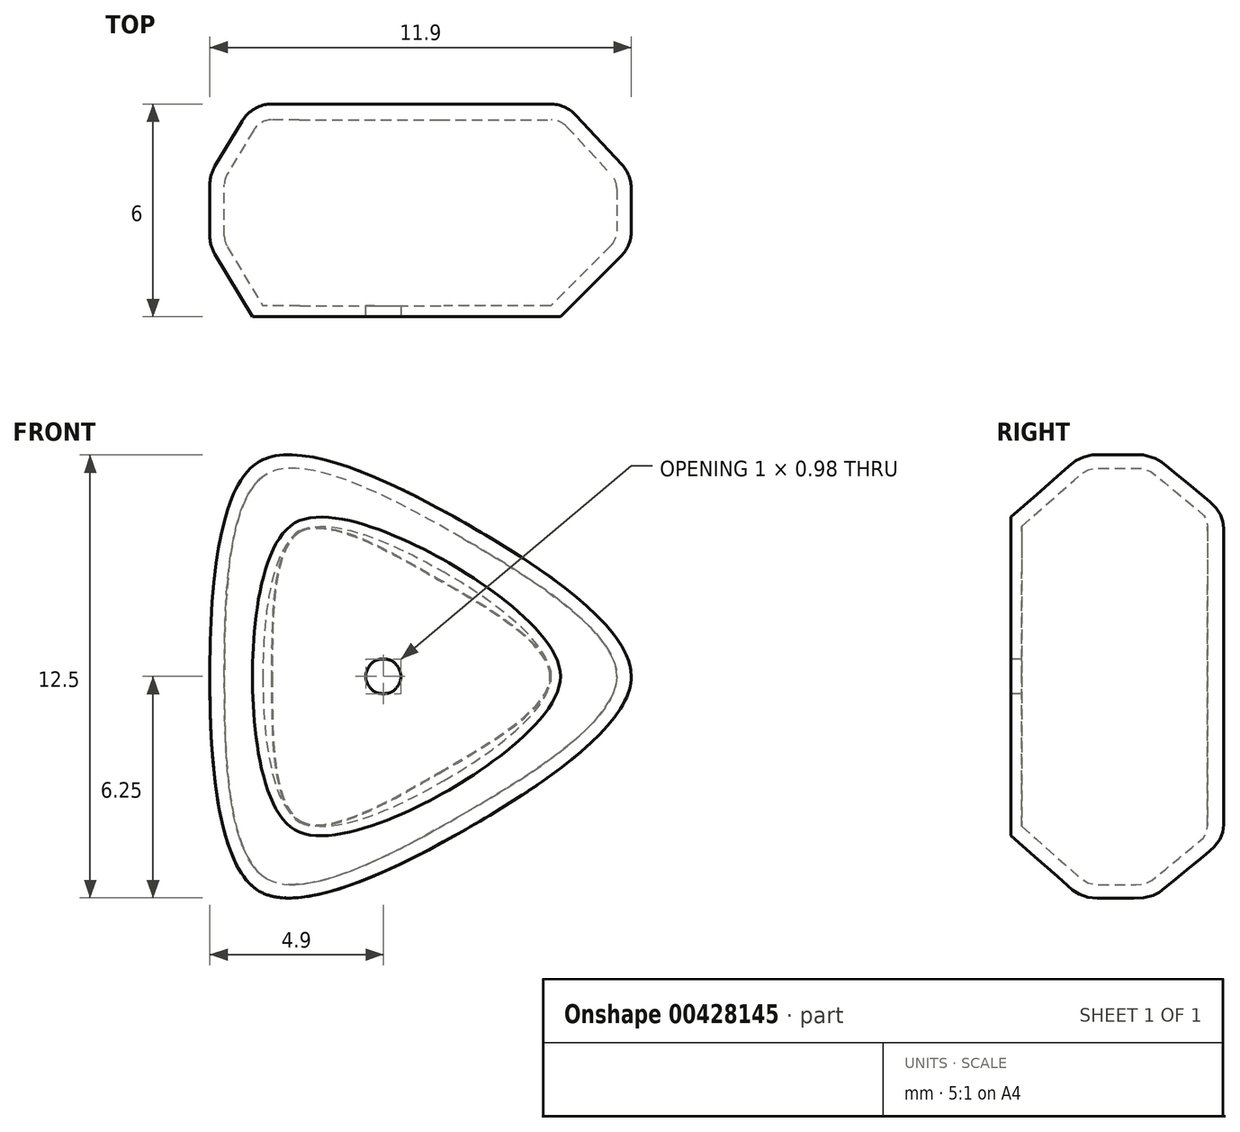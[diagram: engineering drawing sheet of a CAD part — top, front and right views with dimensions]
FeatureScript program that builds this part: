
annotation { "Feature Type Name" : "Feature", "Feature Type Description" : "" }
export const myFeature = defineFeature(function(context is Context, id is Id, definition is map)
    precondition{}
    {
        {
            var Q0;
            Q0=qCreatedBy(makeId("Top.planeOp"),FACE);
            var sketch = newSketch(context, id + "F0", { "sketchPlane" : qUnion([Q0])});
            skLineSegment(sketch, "E0", {"start": v(0, 0) * mm, "end": v(0, 3) * mm});
            skSolve(sketch);
        }
        {
            var Q0;
            Q0=sQuery(id+"F0.wireOp",EDGE,"E0");
            cPlane(context, id + "F1", {"entities" : qUnion([Q0]), "cplaneType" : CPlaneType.LINE_ANGLE, "offset" : 25 * mm, "angle" : 120 * degree, "width" : 150 * mm, "height" : 150 * mm});
        }
        {
            var Q0;
            Q0=sQuery(id+"F0.wireOp",EDGE,"E0");
            cPlane(context, id + "F2", {"entities" : qUnion([Q0]), "cplaneType" : CPlaneType.LINE_ANGLE, "offset" : 25 * mm, "angle" : 120 * degree, "oppositeDirection" : true, "width" : 150 * mm, "height" : 150 * mm});
        }
        {
            var Q0;
            Q0=qCreatedBy(makeId("Top.planeOp"),FACE);
            var sketch = newSketch(context, id + "F3", { "sketchPlane" : qUnion([Q0])});
            skLineSegment(sketch, "E1", {"start": v(0.5, 0) * mm, "end": v(5, 0) * mm});
            skLineSegment(sketch, "E2", {"start": v(7, 2.41) * mm, "end": v(7, 3.6) * mm});
            skLineSegment(sketch, "E3", {"start": v(4.7, 6) * mm, "end": v(0.5, 6) * mm});
            skLineSegment(sketch, "E4", {"start": v(5.44, 5.68) * mm, "end": v(6.73, 4.29) * mm});
            skLineSegment(sketch, "E5", {"start": v(6.7, 1.7) * mm, "end": v(5, 0) * mm});
            skLineSegment(sketch, "E6", {"start": v(0.5, 6) * mm, "end": v(0.5, 5.55) * mm});
            skLineSegment(sketch, "E7", {"start": v(0.5, 5.55) * mm, "end": v(4.74, 5.55) * mm});
            skLineSegment(sketch, "E8", {"start": v(6.6, 3.6) * mm, "end": v(6.6, 2.41) * mm});
            skLineSegment(sketch, "E9", {"start": v(4.72, 0.3) * mm, "end": v(0.5, 0.3) * mm});
            skLineSegment(sketch, "E10", {"start": v(5.18, 5.36) * mm, "end": v(6.43, 4) * mm});
            skLineSegment(sketch, "E11", {"start": v(6.42, 2) * mm, "end": v(4.72, 0.3) * mm});
            skPoint(sketch, "E12.visualSharp", {"position": v(5.14, 6) * mm});
            skArc(sketch, "E12.filletArc", {"start": v(5.44, 5.68) * mm, "mid": v(5.1, 5.92) * mm, "end": v(4.7, 6) * mm});
            skPoint(sketch, "E13.visualSharp", {"position": v(7, 4) * mm});
            skArc(sketch, "E13.filletArc", {"start": v(7, 3.6) * mm, "mid": v(6.93, 3.97) * mm, "end": v(6.73, 4.29) * mm});
            skPoint(sketch, "E14.visualSharp", {"position": v(7, 2) * mm});
            skArc(sketch, "E14.filletArc", {"start": v(6.7, 1.7) * mm, "mid": v(6.92, 2.03) * mm, "end": v(7, 2.41) * mm});
            skPoint(sketch, "E15.visualSharp", {"position": v(5, 5.55) * mm});
            skArc(sketch, "E15.filletArc", {"start": v(5.18, 5.36) * mm, "mid": v(4.98, 5.5) * mm, "end": v(4.74, 5.55) * mm});
            skPoint(sketch, "E16.visualSharp", {"position": v(6.6, 3.84) * mm});
            skArc(sketch, "E16.filletArc", {"start": v(6.6, 3.6) * mm, "mid": v(6.55, 3.82) * mm, "end": v(6.43, 4) * mm});
            skPoint(sketch, "E17.visualSharp", {"position": v(6.6, 2.17) * mm});
            skArc(sketch, "E17.filletArc", {"start": v(6.42, 2) * mm, "mid": v(6.55, 2.19) * mm, "end": v(6.6, 2.41) * mm});
            skLineSegment(sketch, "E18", {"start": v(0.5, 0.3) * mm, "end": v(0.5, 0) * mm});
            skSolve(sketch);
        }
        {
            var Q0;
            Q0=qCreatedBy(makeId("Top.planeOp"),FACE);
            var sketch = newSketch(context, id + "F4", { "sketchPlane" : qUnion([Q0])});
            skLineSegment(sketch, "E19", {"start": v(-0.5, 0) * mm, "end": v(-3.7, 0) * mm});
            skLineSegment(sketch, "E20", {"start": v(-4.9, 2.28) * mm, "end": v(-4.9, 3.72) * mm});
            skLineSegment(sketch, "E21", {"start": v(-4.76, 1.76) * mm, "end": v(-3.7, 0) * mm});
            skLineSegment(sketch, "E22", {"start": v(-3.13, 6) * mm, "end": v(-0.5, 6) * mm});
            skLineSegment(sketch, "E23", {"start": v(-4.76, 4.24) * mm, "end": v(-4, 5.51) * mm});
            skLineSegment(sketch, "E24", {"start": v(-0.5, 0) * mm, "end": v(-0.5, 0.3) * mm});
            skLineSegment(sketch, "E25", {"start": v(-0.5, 0.3) * mm, "end": v(-3.4, 0.3) * mm});
            skLineSegment(sketch, "E26", {"start": v(-4.5, 2.28) * mm, "end": v(-4.5, 3.72) * mm});
            skLineSegment(sketch, "E27", {"start": v(-3.16, 5.55) * mm, "end": v(-0.5, 5.55) * mm});
            skLineSegment(sketch, "E28", {"start": v(-0.5, 5.55) * mm, "end": v(-0.5, 6) * mm});
            skLineSegment(sketch, "E29", {"start": v(-3.66, 5.26) * mm, "end": v(-4.4, 4.03) * mm});
            skLineSegment(sketch, "E30", {"start": v(-4.4, 1.97) * mm, "end": v(-3.4, 0.3) * mm});
            skPoint(sketch, "E31.visualSharp", {"position": v(-3.7, 6) * mm});
            skArc(sketch, "E31.filletArc", {"start": v(-3.13, 6) * mm, "mid": v(-3.63, 5.87) * mm, "end": v(-4, 5.51) * mm});
            skPoint(sketch, "E32.visualSharp", {"position": v(-4.9, 4) * mm});
            skArc(sketch, "E32.filletArc", {"start": v(-4.76, 4.24) * mm, "mid": v(-4.86, 3.99) * mm, "end": v(-4.9, 3.72) * mm});
            skPoint(sketch, "E33.visualSharp", {"position": v(-4.9, 2) * mm});
            skArc(sketch, "E33.filletArc", {"start": v(-4.9, 2.28) * mm, "mid": v(-4.86, 2.01) * mm, "end": v(-4.76, 1.76) * mm});
            skPoint(sketch, "E34.visualSharp", {"position": v(-3.5, 5.55) * mm});
            skArc(sketch, "E34.filletArc", {"start": v(-3.16, 5.55) * mm, "mid": v(-3.45, 5.47) * mm, "end": v(-3.66, 5.26) * mm});
            skPoint(sketch, "E35.visualSharp", {"position": v(-4.5, 3.89) * mm});
            skArc(sketch, "E35.filletArc", {"start": v(-4.4, 4.03) * mm, "mid": v(-4.47, 3.88) * mm, "end": v(-4.5, 3.72) * mm});
            skPoint(sketch, "E36.visualSharp", {"position": v(-4.5, 2.11) * mm});
            skArc(sketch, "E36.filletArc", {"start": v(-4.5, 2.28) * mm, "mid": v(-4.47, 2.12) * mm, "end": v(-4.4, 1.97) * mm});
            skSolve(sketch);
        }
        {
            var Q0;
            Q0=qCreatedBy(id+"F2.planeOp",FACE);
            var sketch = newSketch(context, id + "F5", { "sketchPlane" : qUnion([Q0])});
            skLineSegment(sketch, "E37", {"start": v(0, 0.5) * mm, "end": v(0, 5) * mm});
            skLineSegment(sketch, "E38", {"start": v(-2.41, 7) * mm, "end": v(-3.6, 7) * mm});
            skLineSegment(sketch, "E39", {"start": v(-6, 4.7) * mm, "end": v(-6, 0.5) * mm});
            skLineSegment(sketch, "E40", {"start": v(-5.68, 5.44) * mm, "end": v(-4.29, 6.73) * mm});
            skLineSegment(sketch, "E41", {"start": v(-1.7, 6.7) * mm, "end": v(0, 5) * mm});
            skLineSegment(sketch, "E42", {"start": v(-6, 0.5) * mm, "end": v(-5.55, 0.5) * mm});
            skLineSegment(sketch, "E43", {"start": v(-5.55, 0.5) * mm, "end": v(-5.55, 4.74) * mm});
            skLineSegment(sketch, "E44", {"start": v(-3.6, 6.6) * mm, "end": v(-2.41, 6.6) * mm});
            skLineSegment(sketch, "E45", {"start": v(-0.3, 4.72) * mm, "end": v(-0.3, 0.5) * mm});
            skLineSegment(sketch, "E46", {"start": v(-5.36, 5.18) * mm, "end": v(-4, 6.43) * mm});
            skLineSegment(sketch, "E47", {"start": v(-2, 6.42) * mm, "end": v(-0.3, 4.72) * mm});
            skPoint(sketch, "E48.visualSharp", {"position": v(-6, 5.14) * mm});
            skArc(sketch, "E48.filletArc", {"start": v(-5.68, 5.44) * mm, "mid": v(-5.92, 5.1) * mm, "end": v(-6, 4.7) * mm});
            skPoint(sketch, "E49.visualSharp", {"position": v(-4, 7) * mm});
            skArc(sketch, "E49.filletArc", {"start": v(-3.6, 7) * mm, "mid": v(-3.97, 6.93) * mm, "end": v(-4.29, 6.73) * mm});
            skPoint(sketch, "E50.visualSharp", {"position": v(-2, 7) * mm});
            skArc(sketch, "E50.filletArc", {"start": v(-1.7, 6.7) * mm, "mid": v(-2.03, 6.92) * mm, "end": v(-2.41, 7) * mm});
            skPoint(sketch, "E51.visualSharp", {"position": v(-5.55, 5) * mm});
            skArc(sketch, "E51.filletArc", {"start": v(-5.36, 5.18) * mm, "mid": v(-5.5, 4.98) * mm, "end": v(-5.55, 4.74) * mm});
            skPoint(sketch, "E52.visualSharp", {"position": v(-3.84, 6.6) * mm});
            skArc(sketch, "E52.filletArc", {"start": v(-3.6, 6.6) * mm, "mid": v(-3.82, 6.55) * mm, "end": v(-4, 6.43) * mm});
            skPoint(sketch, "E53.visualSharp", {"position": v(-2.17, 6.6) * mm});
            skArc(sketch, "E53.filletArc", {"start": v(-2, 6.42) * mm, "mid": v(-2.19, 6.55) * mm, "end": v(-2.41, 6.6) * mm});
            skLineSegment(sketch, "E54", {"start": v(-0.3, 0.5) * mm, "end": v(0, 0.5) * mm});
            skSolve(sketch);
        }
        {
            var Q0;
            Q0=qCreatedBy(id+"F2.planeOp",FACE);
            var sketch = newSketch(context, id + "F6", { "sketchPlane" : qUnion([Q0])});
            skLineSegment(sketch, "E55", {"start": v(0, -0.5) * mm, "end": v(0, -3.7) * mm});
            skLineSegment(sketch, "E56", {"start": v(-2.28, -4.9) * mm, "end": v(-3.72, -4.9) * mm});
            skLineSegment(sketch, "E57", {"start": v(-1.76, -4.76) * mm, "end": v(0, -3.7) * mm});
            skLineSegment(sketch, "E58", {"start": v(-6, -3.13) * mm, "end": v(-6, -0.5) * mm});
            skLineSegment(sketch, "E59", {"start": v(-4.24, -4.76) * mm, "end": v(-5.51, -4) * mm});
            skLineSegment(sketch, "E60", {"start": v(0, -0.5) * mm, "end": v(-0.3, -0.5) * mm});
            skLineSegment(sketch, "E61", {"start": v(-0.3, -0.5) * mm, "end": v(-0.3, -3.4) * mm});
            skLineSegment(sketch, "E62", {"start": v(-2.28, -4.5) * mm, "end": v(-3.72, -4.5) * mm});
            skLineSegment(sketch, "E63", {"start": v(-5.55, -3.16) * mm, "end": v(-5.55, -0.5) * mm});
            skLineSegment(sketch, "E64", {"start": v(-5.55, -0.5) * mm, "end": v(-6, -0.5) * mm});
            skLineSegment(sketch, "E65", {"start": v(-5.26, -3.66) * mm, "end": v(-4.03, -4.4) * mm});
            skLineSegment(sketch, "E66", {"start": v(-1.97, -4.4) * mm, "end": v(-0.3, -3.4) * mm});
            skPoint(sketch, "E67.visualSharp", {"position": v(-6, -3.7) * mm});
            skArc(sketch, "E67.filletArc", {"start": v(-6, -3.13) * mm, "mid": v(-5.87, -3.63) * mm, "end": v(-5.51, -4) * mm});
            skPoint(sketch, "E68.visualSharp", {"position": v(-4, -4.9) * mm});
            skArc(sketch, "E68.filletArc", {"start": v(-4.24, -4.76) * mm, "mid": v(-3.99, -4.86) * mm, "end": v(-3.72, -4.9) * mm});
            skPoint(sketch, "E69.visualSharp", {"position": v(-2, -4.9) * mm});
            skArc(sketch, "E69.filletArc", {"start": v(-2.28, -4.9) * mm, "mid": v(-2.01, -4.86) * mm, "end": v(-1.76, -4.76) * mm});
            skPoint(sketch, "E70.visualSharp", {"position": v(-5.55, -3.5) * mm});
            skArc(sketch, "E70.filletArc", {"start": v(-5.55, -3.16) * mm, "mid": v(-5.47, -3.45) * mm, "end": v(-5.26, -3.66) * mm});
            skPoint(sketch, "E71.visualSharp", {"position": v(-3.89, -4.5) * mm});
            skArc(sketch, "E71.filletArc", {"start": v(-4.03, -4.4) * mm, "mid": v(-3.88, -4.47) * mm, "end": v(-3.72, -4.5) * mm});
            skPoint(sketch, "E72.visualSharp", {"position": v(-2.11, -4.5) * mm});
            skArc(sketch, "E72.filletArc", {"start": v(-2.28, -4.5) * mm, "mid": v(-2.12, -4.47) * mm, "end": v(-1.97, -4.4) * mm});
            skSolve(sketch);
        }
        {
            var Q0;
            Q0=qCreatedBy(id+"F1.planeOp",FACE);
            var sketch = newSketch(context, id + "F7", { "sketchPlane" : qUnion([Q0])});
            skLineSegment(sketch, "E73", {"start": v(0, -0.5) * mm, "end": v(0, -5) * mm});
            skLineSegment(sketch, "E74", {"start": v(2.41, -7) * mm, "end": v(3.6, -7) * mm});
            skLineSegment(sketch, "E75", {"start": v(6, -4.7) * mm, "end": v(6, -0.5) * mm});
            skLineSegment(sketch, "E76", {"start": v(5.68, -5.44) * mm, "end": v(4.29, -6.73) * mm});
            skLineSegment(sketch, "E77", {"start": v(1.7, -6.7) * mm, "end": v(0, -5) * mm});
            skLineSegment(sketch, "E78", {"start": v(6, -0.5) * mm, "end": v(5.55, -0.5) * mm});
            skLineSegment(sketch, "E79", {"start": v(5.55, -0.5) * mm, "end": v(5.55, -4.74) * mm});
            skLineSegment(sketch, "E80", {"start": v(3.6, -6.6) * mm, "end": v(2.41, -6.6) * mm});
            skLineSegment(sketch, "E81", {"start": v(0.3, -4.72) * mm, "end": v(0.3, -0.5) * mm});
            skLineSegment(sketch, "E82", {"start": v(5.36, -5.18) * mm, "end": v(4, -6.43) * mm});
            skLineSegment(sketch, "E83", {"start": v(2, -6.42) * mm, "end": v(0.3, -4.72) * mm});
            skPoint(sketch, "E84.visualSharp", {"position": v(6, -5.14) * mm});
            skArc(sketch, "E84.filletArc", {"start": v(5.68, -5.44) * mm, "mid": v(5.92, -5.1) * mm, "end": v(6, -4.7) * mm});
            skPoint(sketch, "E85.visualSharp", {"position": v(4, -7) * mm});
            skArc(sketch, "E85.filletArc", {"start": v(3.6, -7) * mm, "mid": v(3.97, -6.93) * mm, "end": v(4.29, -6.73) * mm});
            skPoint(sketch, "E86.visualSharp", {"position": v(2, -7) * mm});
            skArc(sketch, "E86.filletArc", {"start": v(1.7, -6.7) * mm, "mid": v(2.03, -6.92) * mm, "end": v(2.41, -7) * mm});
            skPoint(sketch, "E87.visualSharp", {"position": v(5.55, -5) * mm});
            skArc(sketch, "E87.filletArc", {"start": v(5.36, -5.18) * mm, "mid": v(5.5, -4.98) * mm, "end": v(5.55, -4.74) * mm});
            skPoint(sketch, "E88.visualSharp", {"position": v(3.84, -6.6) * mm});
            skArc(sketch, "E88.filletArc", {"start": v(3.6, -6.6) * mm, "mid": v(3.82, -6.55) * mm, "end": v(4, -6.43) * mm});
            skPoint(sketch, "E89.visualSharp", {"position": v(2.17, -6.6) * mm});
            skArc(sketch, "E89.filletArc", {"start": v(2, -6.42) * mm, "mid": v(2.19, -6.55) * mm, "end": v(2.41, -6.6) * mm});
            skLineSegment(sketch, "E90", {"start": v(0.3, -0.5) * mm, "end": v(0, -0.5) * mm});
            skSolve(sketch);
        }
        {
            var Q0;
            Q0=qCreatedBy(id+"F1.planeOp",FACE);
            var sketch = newSketch(context, id + "F8", { "sketchPlane" : qUnion([Q0])});
            skLineSegment(sketch, "E91", {"start": v(0, 0.5) * mm, "end": v(0, 3.7) * mm});
            skLineSegment(sketch, "E92", {"start": v(2.28, 4.9) * mm, "end": v(3.72, 4.9) * mm});
            skLineSegment(sketch, "E93", {"start": v(1.76, 4.76) * mm, "end": v(0, 3.7) * mm});
            skLineSegment(sketch, "E94", {"start": v(6, 3.13) * mm, "end": v(6, 0.5) * mm});
            skLineSegment(sketch, "E95", {"start": v(4.24, 4.76) * mm, "end": v(5.51, 4) * mm});
            skLineSegment(sketch, "E96", {"start": v(0, 0.5) * mm, "end": v(0.3, 0.5) * mm});
            skLineSegment(sketch, "E97", {"start": v(0.3, 0.5) * mm, "end": v(0.3, 3.4) * mm});
            skLineSegment(sketch, "E98", {"start": v(2.28, 4.5) * mm, "end": v(3.72, 4.5) * mm});
            skLineSegment(sketch, "E99", {"start": v(5.55, 3.16) * mm, "end": v(5.55, 0.5) * mm});
            skLineSegment(sketch, "E100", {"start": v(5.55, 0.5) * mm, "end": v(6, 0.5) * mm});
            skLineSegment(sketch, "E101", {"start": v(5.26, 3.66) * mm, "end": v(4.03, 4.4) * mm});
            skLineSegment(sketch, "E102", {"start": v(1.97, 4.4) * mm, "end": v(0.3, 3.4) * mm});
            skPoint(sketch, "E103.visualSharp", {"position": v(6, 3.7) * mm});
            skArc(sketch, "E103.filletArc", {"start": v(6, 3.13) * mm, "mid": v(5.87, 3.63) * mm, "end": v(5.51, 4) * mm});
            skPoint(sketch, "E104.visualSharp", {"position": v(4, 4.9) * mm});
            skArc(sketch, "E104.filletArc", {"start": v(4.24, 4.76) * mm, "mid": v(3.99, 4.86) * mm, "end": v(3.72, 4.9) * mm});
            skPoint(sketch, "E105.visualSharp", {"position": v(2, 4.9) * mm});
            skArc(sketch, "E105.filletArc", {"start": v(2.28, 4.9) * mm, "mid": v(2.01, 4.86) * mm, "end": v(1.76, 4.76) * mm});
            skPoint(sketch, "E106.visualSharp", {"position": v(5.55, 3.5) * mm});
            skArc(sketch, "E106.filletArc", {"start": v(5.55, 3.16) * mm, "mid": v(5.47, 3.45) * mm, "end": v(5.26, 3.66) * mm});
            skPoint(sketch, "E107.visualSharp", {"position": v(3.89, 4.5) * mm});
            skArc(sketch, "E107.filletArc", {"start": v(4.03, 4.4) * mm, "mid": v(3.88, 4.47) * mm, "end": v(3.72, 4.5) * mm});
            skPoint(sketch, "E108.visualSharp", {"position": v(2.11, 4.5) * mm});
            skArc(sketch, "E108.filletArc", {"start": v(2.28, 4.5) * mm, "mid": v(2.12, 4.47) * mm, "end": v(1.97, 4.4) * mm});
            skSolve(sketch);
        }
        {
            var Q0;
            Q0=makeQuery(id+"F5.imprint","IMPRINT",FACE,{"disambiguationData":[TD([[makeQuery(id+"F5.imprint","IMPRINT",EDGE,{"derivedFrom":sQuery(id+"F5.wireOp",EDGE,"E37")}),1.0]])]});
            var Q1;
            Q1=makeQuery(id+"F4.imprint","IMPRINT",FACE,{"disambiguationData":[TD([[makeQuery(id+"F4.imprint","IMPRINT",EDGE,{"derivedFrom":sQuery(id+"F4.wireOp",EDGE,"E19")}),-1.0]])]});
            loft(context, id + "F9", {"startCondition" : LoftEndDerivativeType.NORMAL_TO_PROFILE, "startMagnitude" : 1, "endCondition" : LoftEndDerivativeType.NORMAL_TO_PROFILE, "endMagnitude" : 1, "sheetProfilesArray" : [{ "sheetProfileEntities" : qUnion([Q0]) }, { "sheetProfileEntities" : qUnion([Q1]) }]});
        }
        {
            var Q1;
            Q1=makeQuery(id+"F4.imprint","IMPRINT",FACE,{"disambiguationData":[TD([[makeQuery(id+"F4.imprint","IMPRINT",EDGE,{"derivedFrom":sQuery(id+"F4.wireOp",EDGE,"E19")}),-1.0]])]});
            var Q2;
            Q2=makeQuery(id+"F7.imprint","IMPRINT",FACE,{"disambiguationData":[TD([[makeQuery(id+"F7.imprint","IMPRINT",EDGE,{"derivedFrom":sQuery(id+"F7.wireOp",EDGE,"E73")}),1.0]])]});
            loft(context, id + "F10", {"operationType" : NewBodyOperationType.ADD, "startCondition" : LoftEndDerivativeType.NORMAL_TO_PROFILE, "startMagnitude" : 1, "endCondition" : LoftEndDerivativeType.NORMAL_TO_PROFILE, "endMagnitude" : 1, "sheetProfilesArray" : [{ "sheetProfileEntities" : qUnion([Q1]) }, { "sheetProfileEntities" : qUnion([Q2]) }]});
        }
        {
            var Q1;
            Q1=makeQuery(id+"F10.opLoft","CAP_FACE",FACE,{"disambiguationData":[OSD([makeQuery(id+"F7.imprint","IMPRINT",FACE,{"disambiguationData":[TD([[makeQuery(id+"F7.imprint","IMPRINT",EDGE,{"derivedFrom":sQuery(id+"F7.wireOp",EDGE,"E73")}),1.0]])]})])],"isStart":true});
            var Q2;
            Q2=makeQuery(id+"F6.imprint","IMPRINT",FACE,{"disambiguationData":[TD([[makeQuery(id+"F6.imprint","IMPRINT",EDGE,{"derivedFrom":sQuery(id+"F6.wireOp",EDGE,"E55")}),-1.0]])]});
            loft(context, id + "F11", {"operationType" : NewBodyOperationType.ADD, "startCondition" : LoftEndDerivativeType.NORMAL_TO_PROFILE, "startMagnitude" : 1, "endCondition" : LoftEndDerivativeType.NORMAL_TO_PROFILE, "endMagnitude" : 1, "sheetProfilesArray" : [{ "sheetProfileEntities" : qUnion([Q1]) }, { "sheetProfileEntities" : qUnion([Q2]) }]});
        }
        {
            var Q1;
            Q1=makeQuery(id+"F6.imprint","IMPRINT",FACE,{"disambiguationData":[TD([[makeQuery(id+"F6.imprint","IMPRINT",EDGE,{"derivedFrom":sQuery(id+"F6.wireOp",EDGE,"E55")}),-1.0]])]});
            var Q2;
            Q2=makeQuery(id+"F3.imprint","IMPRINT",FACE,{"disambiguationData":[TD([[makeQuery(id+"F3.imprint","IMPRINT",EDGE,{"derivedFrom":sQuery(id+"F3.wireOp",EDGE,"E1")}),1.0]])]});
            loft(context, id + "F12", {"operationType" : NewBodyOperationType.ADD, "startCondition" : LoftEndDerivativeType.NORMAL_TO_PROFILE, "startMagnitude" : 1, "endCondition" : LoftEndDerivativeType.NORMAL_TO_PROFILE, "endMagnitude" : 1, "sheetProfilesArray" : [{ "sheetProfileEntities" : qUnion([Q1]) }, { "sheetProfileEntities" : qUnion([Q2]) }]});
        }
        {
            var Q1;
            Q1=makeQuery(id+"F3.imprint","IMPRINT",FACE,{"disambiguationData":[TD([[makeQuery(id+"F3.imprint","IMPRINT",EDGE,{"derivedFrom":sQuery(id+"F3.wireOp",EDGE,"E1")}),1.0]])]});
            var Q2;
            Q2=makeQuery(id+"F8.imprint","IMPRINT",FACE,{"disambiguationData":[TD([[makeQuery(id+"F8.imprint","IMPRINT",EDGE,{"derivedFrom":sQuery(id+"F8.wireOp",EDGE,"E91")}),-1.0]])]});
            loft(context, id + "F13", {"operationType" : NewBodyOperationType.ADD, "startCondition" : LoftEndDerivativeType.NORMAL_TO_PROFILE, "startMagnitude" : 1, "endCondition" : LoftEndDerivativeType.NORMAL_TO_PROFILE, "endMagnitude" : 1, "sheetProfilesArray" : [{ "sheetProfileEntities" : qUnion([Q1]) }, { "sheetProfileEntities" : qUnion([Q2]) }]});
        }
        {
            var Q1;
            Q1=makeQuery(id+"F5.imprint","IMPRINT",FACE,{"disambiguationData":[TD([[makeQuery(id+"F5.imprint","IMPRINT",EDGE,{"derivedFrom":sQuery(id+"F5.wireOp",EDGE,"E37")}),1.0]])]});
            var Q2;
            Q2=makeQuery(id+"F8.imprint","IMPRINT",FACE,{"disambiguationData":[TD([[makeQuery(id+"F8.imprint","IMPRINT",EDGE,{"derivedFrom":sQuery(id+"F8.wireOp",EDGE,"E91")}),-1.0]])]});
            loft(context, id + "F14", {"operationType" : NewBodyOperationType.ADD, "startCondition" : LoftEndDerivativeType.NORMAL_TO_PROFILE, "startMagnitude" : 1, "endCondition" : LoftEndDerivativeType.NORMAL_TO_PROFILE, "endMagnitude" : 1, "sheetProfilesArray" : [{ "sheetProfileEntities" : qUnion([Q1]) }, { "sheetProfileEntities" : qUnion([Q2]) }]});
        }
        {
            var Q0;
            {var subQ0=sQuery(id+"F8.wireOp",EDGE,"E103.filletArc");var subQ1=sQuery(id+"F8.wireOp",EDGE,"E100");var subQ2=sQuery(id+"F8.wireOp",EDGE,"E94");var subQ3=sQuery(id+"F5.wireOp",EDGE,"E48.filletArc");var subQ4=sQuery(id+"F5.wireOp",EDGE,"E42");var subQ5=sQuery(id+"F5.wireOp",EDGE,"E39");var subQ6=sQuery(id+"F3.wireOp",EDGE,"E12.filletArc");var subQ7=sQuery(id+"F3.wireOp",EDGE,"E6");var subQ8=sQuery(id+"F3.wireOp",EDGE,"E3");var subQ9=sQuery(id+"F6.wireOp",EDGE,"E67.filletArc");var subQ10=sQuery(id+"F6.wireOp",EDGE,"E64");var subQ11=sQuery(id+"F6.wireOp",EDGE,"E58");var subQ12=sQuery(id+"F7.wireOp",EDGE,"E84.filletArc");var subQ13=sQuery(id+"F7.wireOp",EDGE,"E78");var subQ14=sQuery(id+"F7.wireOp",EDGE,"E75");var subQ15=sQuery(id+"F4.wireOp",EDGE,"E31.filletArc");var subQ16=sQuery(id+"F4.wireOp",EDGE,"E28");var subQ17=sQuery(id+"F4.wireOp",EDGE,"E22");Q0=makeQuery(id+"F14.boolean.opBoolean","MERGE",FACE,{"derivedFrom":[makeQuery(id+"F13.boolean.opBoolean","MERGE",FACE,{"derivedFrom":[makeQuery(id+"F12.boolean.opBoolean","MERGE",FACE,{"derivedFrom":[makeQuery(id+"F11.boolean.opBoolean","MERGE",FACE,{"derivedFrom":[makeQuery(id+"F10.boolean.opBoolean","MERGE",FACE,{"derivedFrom":[makeQuery(id+"F9.opLoft","SWEPT_FACE",FACE,{"disambiguationData":[OSD([subQ17,subQ16,subQ15,subQ5,subQ4,subQ3])]}),makeQuery(id+"F10.opLoft","SWEPT_FACE",FACE,{"disambiguationData":[OSD([subQ17,subQ16,subQ15,subQ14,subQ13,subQ12])]})]}),makeQuery(id+"F11.opLoft","SWEPT_FACE",FACE,{"disambiguationData":[OSD([subQ11,subQ10,subQ9,subQ14,subQ13,subQ12])]})]}),makeQuery(id+"F12.opLoft","SWEPT_FACE",FACE,{"disambiguationData":[OSD([subQ8,subQ7,subQ6,subQ11,subQ10,subQ9])]})]}),makeQuery(id+"F13.opLoft","SWEPT_FACE",FACE,{"disambiguationData":[OSD([subQ8,subQ7,subQ6,subQ2,subQ1,subQ0])]})]}),makeQuery(id+"F14.opLoft","SWEPT_FACE",FACE,{"disambiguationData":[OSD([subQ5,subQ4,subQ3,subQ2,subQ1,subQ0])]})]});}
            var sketch = newSketch(context, id + "F15", { "sketchPlane" : qUnion([Q0])});
            skCircle(sketch, "E109", {"center": v(0, 0) * mm, "radius": 1.08 * mm});
            skSolve(sketch);
        }
        {
            var Q0;
            {var subQ6=sQuery(id+"F4.wireOp",EDGE,"E28");var subQ7=sQuery(id+"F4.wireOp",EDGE,"E22");var subQ8=sQuery(id+"F5.wireOp",EDGE,"E42");var subQ9=sQuery(id+"F5.wireOp",EDGE,"E39");Q0=makeQuery(id+"F15.imprint","IMPRINT",FACE,{"disambiguationData":[TD([[makeQuery(id+"F15.imprint","IMPRINT",EDGE,{"derivedFrom":makeQuery(id+"F9.opLoft","SWEPT_EDGE",EDGE,{"disambiguationData":[OSD([subQ7,subQ6,subQ9,subQ8])]})}),-1.0]])]});}
            extrude(context, id + "F16", {"entities" : qUnion([Q0]), "operationType" : NewBodyOperationType.ADD, "oppositeDirection" : true, "depth" : 0.45 * mm});
        }
    });
